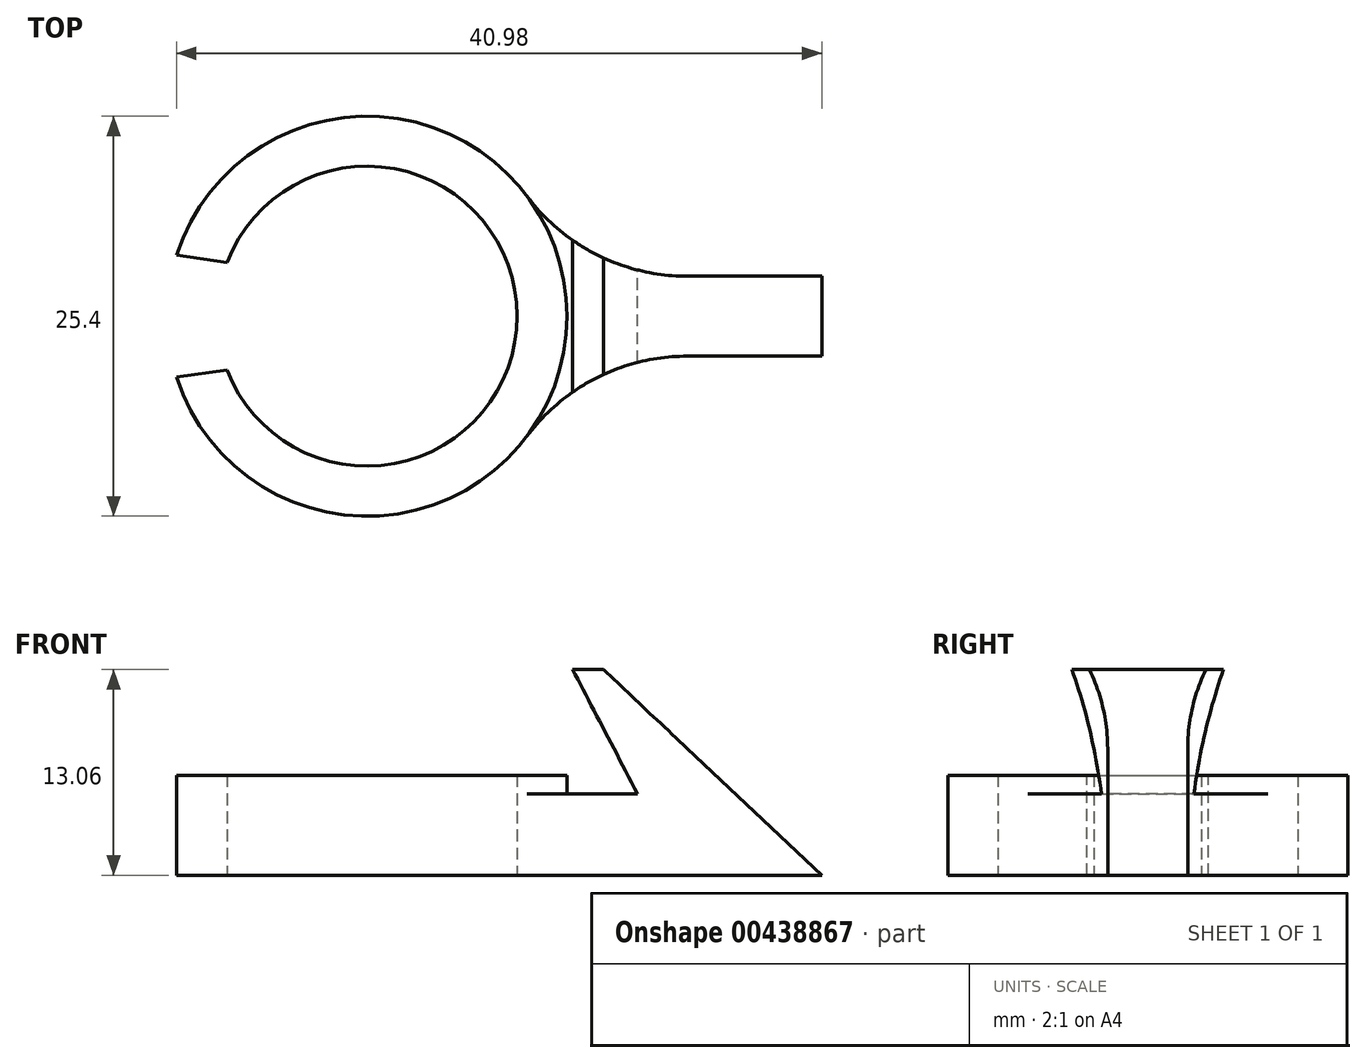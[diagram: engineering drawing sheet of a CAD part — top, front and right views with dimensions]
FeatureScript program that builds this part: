
annotation { "Feature Type Name" : "Feature", "Feature Type Description" : "" }
export const myFeature = defineFeature(function(context is Context, id is Id, definition is map)
    precondition{}
    {
        {
            var Q0;
            Q0=qCreatedBy(makeId("Top.planeOp"),FACE);
            var sketch = newSketch(context, id + "F0", { "sketchPlane" : qUnion([Q0])});
            skCircle(sketch, "E0", {"center": v(0, 0) * mm, "radius": 9.53 * mm});
            skCircle(sketch, "E1", {"center": v(0, 0) * mm, "radius": 12.7 * mm});
            skSolve(sketch);
        }
        {
            var Q0;
            Q0=qCreatedBy(makeId("Right.planeOp"),FACE);
            cPlane(context, id + "F1", {"entities" : qUnion([Q0]), "cplaneType" : CPlaneType.OFFSET, "offset" : 12.7 * mm, "width" : 152.4 * mm, "height" : 152.4 * mm});
        }
        {
            var Q0;
            Q0 = qSketchRegion(id + "F0", true);
            extrude(context, id + "F2", {"entities" : qUnion([Q0]), "depth" : 6.35 * mm});
        }
        {
            var Q0;
            Q0=makeQuery(id+"F2.opExtrude","CAP_FACE",FACE,{"disambiguationData":[OSD([sQuery(id+"F0.wireOp",EDGE,"E0"),sQuery(id+"F0.wireOp",EDGE,"E1")])],"isStart":false});
            var sketch = newSketch(context, id + "F3", { "sketchPlane" : qUnion([Q0])});
            skLineSegment(sketch, "E2", {"start": v(0, 0) * mm, "end": v(-12.7, 0) * mm, "construction": true});
            skArc(sketch, "E3", {"start": v(-11.05, 6.26) * mm, "mid": v(-12.7, 0) * mm, "end": v(-11.05, -6.26) * mm});
            skLineSegment(sketch, "E4", {"start": v(-12.1, -3.87) * mm, "end": v(2.02, -1.87) * mm});
            skLineSegment(sketch, "E5.MirrorCS", {"start": v(-12.1, 3.87) * mm, "end": v(2.02, 1.87) * mm});
            skLineSegment(sketch, "E6", {"start": v(2.02, -4.94) * mm, "end": v(2.02, 3.55) * mm});
            skPoint(sketch, "E7.orphan", {"position": v(15.28, 0) * mm});
            skArc(sketch, "E8", {"start": v(-12.1, 3.87) * mm, "mid": v(-12.7, 0) * mm, "end": v(-12.1, -3.87) * mm});
            skSolve(sketch);
        }
        {
            var Q0;
            Q0 = qSketchRegion(id + "F3", true);
            extrude(context, id + "F4", {"entities" : qUnion([Q0]), "operationType" : NewBodyOperationType.REMOVE, "oppositeDirection" : true, "depth" : 25.4 * mm});
        }
        {
            var Q0;
            Q0=qCreatedBy(makeId("Front.planeOp"),FACE);
            var sketch = newSketch(context, id + "F5", { "sketchPlane" : qUnion([Q0])});
            skLineSegment(sketch, "E9", {"start": v(10.7, 0) * mm, "end": v(28.88, 0) * mm});
            skLineSegment(sketch, "E10", {"start": v(13.06, 13.06) * mm, "end": v(17.18, 5.16) * mm});
            skLineSegment(sketch, "E11", {"start": v(17.18, 5.16) * mm, "end": v(10.56, 5.16) * mm});
            skLineSegment(sketch, "E12", {"start": v(10.7, 0) * mm, "end": v(10.56, 5.16) * mm});
            skLineSegment(sketch, "E13", {"start": v(13.06, 13.06) * mm, "end": v(15.01, 13.06) * mm});
            skLineSegment(sketch, "E14", {"start": v(15.01, 13.06) * mm, "end": v(28.88, 0) * mm});
            skSolve(sketch);
        }
        {
            var Q0;
            Q0 = qSketchRegion(id + "F5", true);
            extrude(context, id + "F6", {"entities" : qUnion([Q0]), "operationType" : NewBodyOperationType.ADD, "depth" : 2.54 * mm, "hasSecondDirection" : true, "secondDirectionOppositeDirection" : true, "secondDirectionDepth" : 2.54 * mm});
        }
        {
            var Q0;
            Q0=makeQuery(id+"F6.boolean.opBoolean","INTERSECT",EDGE,{"derivedFrom":[makeQuery(id+"F2.opExtrude","SWEPT_FACE",FACE,{"disambiguationData":[OSD([sQuery(id+"F0.wireOp",EDGE,"E1")])]}),makeQuery(id+"F6.opExtrude","CAP_FACE",FACE,{"disambiguationData":[OSD([sQuery(id+"F5.wireOp",EDGE,"E9"),sQuery(id+"F5.wireOp",EDGE,"E10"),sQuery(id+"F5.wireOp",EDGE,"E11"),sQuery(id+"F5.wireOp",EDGE,"E12"),sQuery(id+"F5.wireOp",EDGE,"E13"),sQuery(id+"F5.wireOp",EDGE,"E14")])],"isStart":false})]});
            fillet(context, id + "F7", {"entities" : qUnion([Q0]), "radius" : 12.7 * mm, "tangentPropagation" : true, "allowEdgeOverflow" : false});
        }
        {
            var Q0;
            Q0=makeQuery(id+"F6.boolean.opBoolean","INTERSECT",EDGE,{"derivedFrom":[makeQuery(id+"F2.opExtrude","SWEPT_FACE",FACE,{"disambiguationData":[OSD([sQuery(id+"F0.wireOp",EDGE,"E1")])]}),makeQuery(id+"F6.opExtrude","CAP_FACE",FACE,{"disambiguationData":[OSD([sQuery(id+"F5.wireOp",EDGE,"E9"),sQuery(id+"F5.wireOp",EDGE,"E10"),sQuery(id+"F5.wireOp",EDGE,"E11"),sQuery(id+"F5.wireOp",EDGE,"E12"),sQuery(id+"F5.wireOp",EDGE,"E13"),sQuery(id+"F5.wireOp",EDGE,"E14")])],"isStart":true})]});
            fillet(context, id + "F8", {"entities" : qUnion([Q0]), "radius" : 12.7 * mm, "tangentPropagation" : true, "allowEdgeOverflow" : false});
        }
    });
